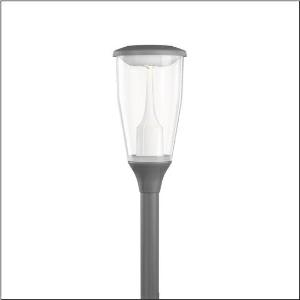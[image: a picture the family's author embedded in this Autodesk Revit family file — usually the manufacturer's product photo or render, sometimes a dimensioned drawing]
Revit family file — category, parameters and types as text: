
# Revit family: dl_11_iq___st1_2a_5xa5565ef14hp00022_07bc
name_source: partatom
category: Lighting Fixtures
units: mm (PartAtom-declared; Revit-internal decimal feet)

## family parameters
Cut with Voids When Loaded = No
Host = Face
Light Source = No
Part Type = Normal
Room Calculation Point = No
Round Connector Dimension = Use Diameter
Shared = No

## types (1)
- --- (1 x LED, 4840 lm, 33.6 W, 3000K)
    Apparent Load = 34 VA
    CIE Flux Codes = 33 63 91 94 100
    Color Rendering = 70
    Color Temperature = 3000K
    Default Elevation = 1800 mm
    Description = DL 11 iQ, mast luminaire, Module 540 iQ-SR, primary light control with 3 zone facetted reflector, of plastic, silver coated, highly specular, structured, primary optical cover: cover, of PMMA, transparent, light distribution: ST1.2a, light emission: direct distribution, primary light characteristic: asymmetric, installation type: post-top, LED, High Power LED, light colour: 730, colour temperature: 3000K, control: Street-Remote, Auto-Match, Temp-Guard, Lumen-Switch, Night-Set, Smart-Wire, Light-Fading, Desk-Remote (wireless, voltage-free reading and setting of iQ features in the workshop via application-optimized NFC function/RFID function), optimised constant luminous flux control (CLO 2.0), mains connection: 220..240V, AC, 50/60Hz, connection cable pre-assembled, cable length: 5,5m, start of lifetime: 34W, end of service life: 36W, luminaire housing, upper part, of diecast aluminium, coated, Siteco® metallic grey (DB 702S), spigot size: 60mm (post-top), post-top mast mounting element, of diecast aluminium, coated, Siteco® metallic grey (DB 702S), Module 540 iQ-SR, traffic white (RAL 9016), equipment: Power, protection rating (complete): IP66, insulation class (complete): insulation class II (safety insulation), certification: CE, ENEC, ENEC+, VDE, packaging unit: 1 piece

Light Distribution: ST1.2a
    Height = 665 mm
    Lamp = 1 x LED
    Lamp Light Flux = 4840 lm
    Lamp Power = 33.6 W
    Lamp count = 1
    Length = 334 mm
    Luminous efficacy = 144 lm/W
    Manufacturer = Siteco
    ModVariant = No
    Model = 5XA5565EF14HP00022
    Number of Poles = 1
    OnlyDefault = Yes
    Power Factor = 1
    Product Name = DL 11 iQ | ST1.2a
    Product group = mast luminaire | pylon top
    ProductGroupID = 6100
    Protection Class = Protection class II
    Protection Degree = IP 66
    RLX_Detail_Level = 1
    RLX_Emergency_Light_Flux = 0 lm
    RLX_Emergency_Type = 0
    RLX_Emergency_Type_DB = No
    RlxData = <blob elided: 156909 chars, md5=611b3a31>
    Socket = socket
    Standby Power = 0 W
    System Light Flux = 4840 lm
    System Power = 34 W
    Type Comments = factory setting: luminous flux: 100 % | dim-lin: 254 | 695 mA
    Type Image = l_1258354.jpg
    URL = http://relux.com
    VarID = @adj_020073
    Voltage = 0 V
    Weight = 0.00 kg
    Width = 0 mm  [stored 0 ft]

note: [stored X ft] marks values corroborated as IEEE doubles in the binary element streams (Revit-internal decimal feet)

## geometry (parser evidence)
native form markers: Blend x4, Sweep x10
no freeform markers — native parametric forms only
